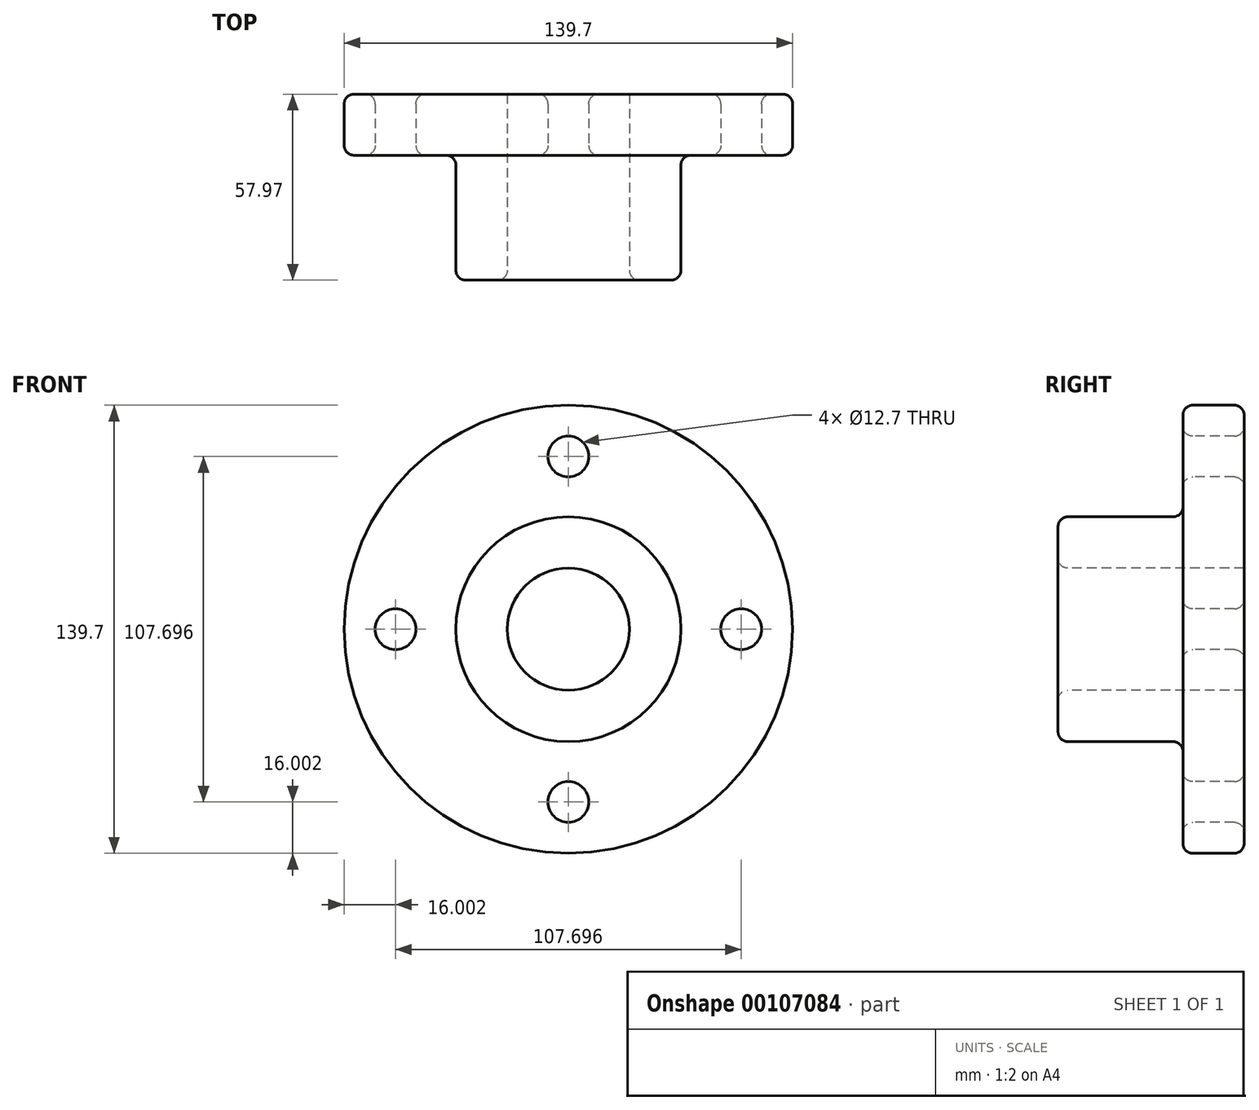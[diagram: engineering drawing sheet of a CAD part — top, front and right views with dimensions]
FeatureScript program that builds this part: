
annotation { "Feature Type Name" : "Feature", "Feature Type Description" : "" }
export const myFeature = defineFeature(function(context is Context, id is Id, definition is map)
    precondition{}
    {
        {
            var Q0;
            Q0=qCreatedBy(makeId("Front.planeOp"),FACE);
            var sketch = newSketch(context, id + "F0", { "sketchPlane" : qUnion([Q0])});
            skCircle(sketch, "E0", {"center": v(0, 0) * mm, "radius": 69.85 * mm});
            skSolve(sketch);
        }
        {
            var Q0;
            Q0 = qSketchRegion(id + "F0", true);
            extrude(context, id + "F1", {"entities" : qUnion([Q0]), "endBound" : BoundingType.SYMMETRIC, "depth" : 19.05 * mm});
        }
        {
            var Q0;
            Q0=qCreatedBy(makeId("Front.planeOp"),FACE);
            var sketch = newSketch(context, id + "F2", { "sketchPlane" : qUnion([Q0])});
            skCircle(sketch, "E1", {"center": v(0, 0) * mm, "radius": 35.05 * mm});
            skSolve(sketch);
        }
        {
            var Q0;
            Q0 = qSketchRegion(id + "F2", true);
            extrude(context, id + "F3", {"entities" : qUnion([Q0]), "operationType" : NewBodyOperationType.ADD, "oppositeDirection" : true, "depth" : 5.4 * mm, "hasSecondDirection" : true, "secondDirectionOppositeDirection" : false, "secondDirectionDepth" : 48.44 * mm});
        }
        {
            var Q0;
            Q0=makeQuery(id+"F3.boolean.opBoolean","INTERSECT",EDGE,{"derivedFrom":[makeQuery(id+"F1.opExtrude","CAP_FACE",FACE,{"disambiguationData":[OSD([sQuery(id+"F0.wireOp",EDGE,"E0")])],"isStart":false}),makeQuery(id+"F3.opExtrude","SWEPT_FACE",FACE,{"disambiguationData":[OSD([sQuery(id+"F2.wireOp",EDGE,"E1")])]})]});
            fillet(context, id + "F4", {"entities" : qUnion([Q0]), "radius" : 3.05 * mm, "tangentPropagation" : true, "allowEdgeOverflow" : false});
        }
        {
            var Q0;
            Q0=qCreatedBy(makeId("Front.planeOp"),FACE);
            var sketch = newSketch(context, id + "F5", { "sketchPlane" : qUnion([Q0])});
            skCircle(sketch, "E2", {"center": v(0, 0) * mm, "radius": 53.85 * mm});
            skSolve(sketch);
        }
        {
            var Q0;
            Q0=qCreatedBy(makeId("Front.planeOp"),FACE);
            var sketch = newSketch(context, id + "F6", { "sketchPlane" : qUnion([Q0])});
            skCircle(sketch, "E3", {"center": v(0, 53.85) * mm, "radius": 6.35 * mm});
            skCircle(sketch, "E4", {"center": v(53.85, 0) * mm, "radius": 6.35 * mm});
            skCircle(sketch, "E5", {"center": v(-53.85, 0) * mm, "radius": 6.35 * mm});
            skCircle(sketch, "E6", {"center": v(0, -53.85) * mm, "radius": 6.35 * mm});
            skSolve(sketch);
        }
        {
            var Q0;
            Q0 = qSketchRegion(id + "F6", true);
            extrude(context, id + "F7", {"entities" : qUnion([Q0]), "operationType" : NewBodyOperationType.REMOVE, "endBound" : BoundingType.SYMMETRIC, "oppositeDirection" : true, "depth" : 50.8 * mm});
        }
        {
            var Q0;
            Q0=makeQuery(id+"F7.boolean.opBoolean","INTERSECT",EDGE,{"derivedFrom":[makeQuery(id+"F1.opExtrude","CAP_FACE",FACE,{"disambiguationData":[OSD([sQuery(id+"F0.wireOp",EDGE,"E0")])],"isStart":false}),makeQuery(id+"F7.opExtrude","SWEPT_FACE",FACE,{"disambiguationData":[OSD([sQuery(id+"F6.wireOp",EDGE,"E5")])]})]});
            var Q1;
            Q1=makeQuery(id+"F7.boolean.opBoolean","INTERSECT",EDGE,{"derivedFrom":[makeQuery(id+"F1.opExtrude","CAP_FACE",FACE,{"disambiguationData":[OSD([sQuery(id+"F0.wireOp",EDGE,"E0")])],"isStart":false}),makeQuery(id+"F7.opExtrude","SWEPT_FACE",FACE,{"disambiguationData":[OSD([sQuery(id+"F6.wireOp",EDGE,"E3")])]})]});
            var Q2;
            Q2=makeQuery(id+"F7.boolean.opBoolean","INTERSECT",EDGE,{"derivedFrom":[makeQuery(id+"F1.opExtrude","CAP_FACE",FACE,{"disambiguationData":[OSD([sQuery(id+"F0.wireOp",EDGE,"E0")])],"isStart":false}),makeQuery(id+"F7.opExtrude","SWEPT_FACE",FACE,{"disambiguationData":[OSD([sQuery(id+"F6.wireOp",EDGE,"E4")])]})]});
            var Q3;
            Q3=makeQuery(id+"F7.boolean.opBoolean","INTERSECT",EDGE,{"derivedFrom":[makeQuery(id+"F1.opExtrude","CAP_FACE",FACE,{"disambiguationData":[OSD([sQuery(id+"F0.wireOp",EDGE,"E0")])],"isStart":false}),makeQuery(id+"F7.opExtrude","SWEPT_FACE",FACE,{"disambiguationData":[OSD([sQuery(id+"F6.wireOp",EDGE,"E6")])]})]});
            var Q4;
            Q4=makeQuery(id+"F7.boolean.opBoolean","INTERSECT",EDGE,{"derivedFrom":[makeQuery(id+"F1.opExtrude","CAP_FACE",FACE,{"disambiguationData":[OSD([sQuery(id+"F0.wireOp",EDGE,"E0")])],"isStart":true}),makeQuery(id+"F7.opExtrude","SWEPT_FACE",FACE,{"disambiguationData":[OSD([sQuery(id+"F6.wireOp",EDGE,"E4")])]})]});
            var Q5;
            Q5=makeQuery(id+"F7.boolean.opBoolean","INTERSECT",EDGE,{"derivedFrom":[makeQuery(id+"F1.opExtrude","CAP_FACE",FACE,{"disambiguationData":[OSD([sQuery(id+"F0.wireOp",EDGE,"E0")])],"isStart":true}),makeQuery(id+"F7.opExtrude","SWEPT_FACE",FACE,{"disambiguationData":[OSD([sQuery(id+"F6.wireOp",EDGE,"E3")])]})]});
            var Q6;
            Q6=makeQuery(id+"F7.boolean.opBoolean","INTERSECT",EDGE,{"derivedFrom":[makeQuery(id+"F1.opExtrude","CAP_FACE",FACE,{"disambiguationData":[OSD([sQuery(id+"F0.wireOp",EDGE,"E0")])],"isStart":true}),makeQuery(id+"F7.opExtrude","SWEPT_FACE",FACE,{"disambiguationData":[OSD([sQuery(id+"F6.wireOp",EDGE,"E5")])]})]});
            var Q7;
            Q7=makeQuery(id+"F7.boolean.opBoolean","INTERSECT",EDGE,{"derivedFrom":[makeQuery(id+"F1.opExtrude","CAP_FACE",FACE,{"disambiguationData":[OSD([sQuery(id+"F0.wireOp",EDGE,"E0")])],"isStart":true}),makeQuery(id+"F7.opExtrude","SWEPT_FACE",FACE,{"disambiguationData":[OSD([sQuery(id+"F6.wireOp",EDGE,"E6")])]})]});
            fillet(context, id + "F8", {"entities" : qUnion([Q0, Q1, Q2, Q3, Q4, Q5, Q6, Q7]), "radius" : 3.05 * mm, "tangentPropagation" : true, "allowEdgeOverflow" : false});
        }
        {
            var Q0;
            Q0=qCreatedBy(makeId("Front.planeOp"),FACE);
            var sketch = newSketch(context, id + "F9", { "sketchPlane" : qUnion([Q0])});
            skCircle(sketch, "E7", {"center": v(0, 0) * mm, "radius": 19.04 * mm});
            skSolve(sketch);
        }
        {
            var Q0;
            Q0 = qSketchRegion(id + "F9", true);
            extrude(context, id + "F10", {"entities" : qUnion([Q0]), "operationType" : NewBodyOperationType.REMOVE, "endBound" : BoundingType.SYMMETRIC, "oppositeDirection" : true, "depth" : 101.6 * mm});
        }
        {
            var Q0;
            Q0=makeQuery(id+"F10.boolean.opBoolean","INTERSECT",EDGE,{"derivedFrom":[makeQuery(id+"F3.opExtrude","CAP_FACE",FACE,{"disambiguationData":[OSD([sQuery(id+"F2.wireOp",EDGE,"E1")])],"isStart":true}),makeQuery(id+"F10.opExtrude","SWEPT_FACE",FACE,{"disambiguationData":[OSD([sQuery(id+"F9.wireOp",EDGE,"E7")])]})]});
            fillet(context, id + "F11", {"entities" : qUnion([Q0]), "radius" : 3.05 * mm, "tangentPropagation" : true, "allowEdgeOverflow" : false});
        }
        {
            var Q0;
            Q0=makeQuery(id+"F3.opExtrude","CAP_EDGE",EDGE,{"disambiguationData":[OSD([sQuery(id+"F2.wireOp",EDGE,"E1")])],"isStart":true});
            var Q1;
            Q1=makeQuery(id+"F1.opExtrude","CAP_EDGE",EDGE,{"disambiguationData":[OSD([sQuery(id+"F0.wireOp",EDGE,"E0")])],"isStart":false});
            var Q2;
            Q2=makeQuery(id+"F1.opExtrude","CAP_EDGE",EDGE,{"disambiguationData":[OSD([sQuery(id+"F0.wireOp",EDGE,"E0")])],"isStart":true});
            fillet(context, id + "F12", {"entities" : qUnion([Q0, Q1, Q2]), "radius" : 3.05 * mm, "tangentPropagation" : true, "allowEdgeOverflow" : false});
        }
    });
